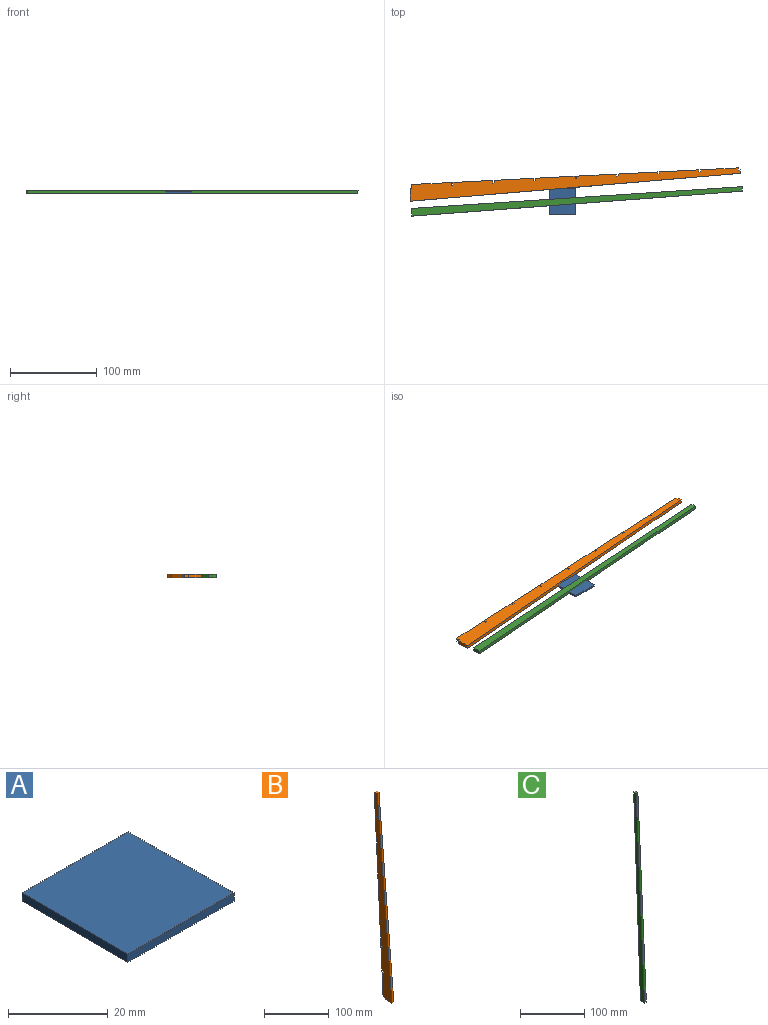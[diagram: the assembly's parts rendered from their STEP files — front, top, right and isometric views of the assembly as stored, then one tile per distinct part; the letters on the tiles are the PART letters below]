
ASSEMBLY  parts=3 mates=2
PART A: 6 faces, bbox 30x30x2 mm
  f0: plane 30x2mm, normal (-1,0,0), area 60mm2, adj f1,f3,f4,f5
  f1: plane 30x2mm, normal (0,-1,0), area 60mm2, adj f0,f2,f4,f5
  f2: plane 30x2mm, normal (1,0,0), area 60mm2, adj f1,f3,f4,f5
  f3: plane 30x2mm, normal (0,1,0), area 60mm2, adj f0,f2,f4,f5
  f4: plane 30x30mm, normal (0,0,1), area 900mm2, adj f0,f1,f2,f3
  f5: plane 30x30mm, normal (0,0,-1), area 900mm2, adj f0,f1,f2,f3
PART B: 38 faces, bbox 5.5x39.9x381.5 mm
  f0: plane 14.29x4mm, normal (0,0,-1), area 57.2mm2, adj f1,f5,f23,f37
  f1: plane 380.01x38.38mm, normal (1,0,0), area 4815.4mm2, adj f0,f2,f3,f4,f6,f7,f8,f9
  f2: plane 4x3.85mm, normal (0,0,1), area 15.4mm2, adj f1,f5,f22,f37
  f3: plane 4x2.7mm, normal (0,0,1), area 10.8mm2, adj f1,f5,f28,f29
  f4: plane 4x1.88mm, normal (0,0,1), area 7.5mm2, adj f1,f5,f34,f35
  f5: plane 381.51x39.88mm, normal (-1,0,0), area 4816mm2, adj f0,f2,f3,f4,f6,f7,f8,f9
  f6: plane 4x2.6mm, normal (0,0,1), area 10.4mm2, adj f1,f5,f21,f22
  f7: plane 4.76x4mm, normal (0,0,-1), area 19mm2, adj f1,f5,f23,f24
  f8: plane 4x3.43mm, normal (0,0,1), area 13.7mm2, adj f1,f5,f24,f25
  f9: plane 4x3.4mm, normal (0,0,-1), area 13.6mm2, adj f1,f5,f25,f26
  f10: plane 4x3.03mm, normal (0,0,-1), area 12.1mm2, adj f1,f5,f27,f28
  f11: plane 4x3.07mm, normal (0,0,1), area 12.3mm2, adj f1,f5,f26,f27
  f12: plane 4x2.66mm, normal (0,0,-1), area 10.7mm2, adj f1,f5,f29,f30
  f13: plane 4x2.62mm, normal (0,0,-1), area 10.5mm2, adj f1,f5,f31,f32
  f14: plane 4x2.66mm, normal (0,0,1), area 10.6mm2, adj f1,f5,f30,f31
  f15: plane 4x2.24mm, normal (0,0,-1), area 9mm2, adj f1,f5,f33,f34
  f16: plane 4x2.27mm, normal (0,0,1), area 9.1mm2, adj f1,f5,f32,f33
  f17: plane 4x1.85mm, normal (0,0,-1), area 7.4mm2, adj f1,f5,f35,f36
  f18: plane 4x2.12mm, normal (0,0,-1), area 8.5mm2, adj f1,f5,f20,f21
  f19: plane 4x2.15mm, normal (0,0,1), area 8.6mm2, adj f1,f5,f20,f36
  f20: plane 4x2mm, normal (0,1,-0.07), area 8mm2, adj f1,f5,f18,f19
  f21: extruded ~43.5x4mm, area 174.2mm2, adj f1,f5,f6,f18
  f22: plane 4x2mm, normal (0,1,-0.07), area 8mm2, adj f1,f2,f5,f6
  f23: plane 4x2mm, normal (0,1,-0.07), area 8mm2, adj f0,f1,f5,f7
  f24: extruded ~45.5x4mm, area 182.2mm2, adj f1,f5,f7,f8
  f25: plane 4x2mm, normal (0,1,-0.07), area 8mm2, adj f1,f5,f8,f9
  f26: extruded ~45.5x4mm, area 182.2mm2, adj f1,f5,f9,f11
  f27: plane 4x2mm, normal (0,1,-0.07), area 8mm2, adj f1,f5,f10,f11
  f28: extruded ~45.5x4mm, area 182.2mm2, adj f1,f3,f5,f10
  f29: plane 4x2mm, normal (0,1,-0.07), area 8mm2, adj f1,f3,f5,f12
  f30: extruded ~45.5x4mm, area 182.2mm2, adj f1,f5,f12,f14
  f31: plane 4x2mm, normal (0,1,-0.07), area 8mm2, adj f1,f5,f13,f14
  f32: extruded ~45.5x4mm, area 182.2mm2, adj f1,f5,f13,f16
  f33: plane 4x2mm, normal (0,1,-0.07), area 8mm2, adj f1,f5,f15,f16
  f34: extruded ~45.5x4mm, area 182.2mm2, adj f1,f4,f5,f15
  f35: plane 4x2mm, normal (0,1,-0.07), area 8mm2, adj f1,f4,f5,f17
  f36: extruded ~45.5x4mm, area 182.2mm2, adj f1,f5,f17,f19
  f37: extruded ~380x32.07mm, area 1525.4mm2, adj f0,f1,f2,f5
PART C: 6 faces, bbox 14x33.9x380.1 mm
  f0: extruded ~380.11x28.68mm, area 1524.8mm2, adj f1,f3,f4,f5
  f1: plane 8.9x4mm, normal (-0.03,0,-1), area 35.6mm2, adj f0,f2,f4,f5
  f2: extruded ~380.11x24.98mm, area 1523.8mm2, adj f1,f3,f4,f5
  f3: plane 5.21x4mm, normal (0.03,0,1), area 20.8mm2, adj f0,f2,f4,f5
  f4: plane 380x33.89mm, normal (-1,0,0.03), area 2727.1mm2, adj f0,f1,f2,f3
  f5: plane 380x33.89mm, normal (1,0,-0.03), area 2727.1mm2, adj f0,f1,f2,f3
PLACE A at identity fixed
PLACE B rot(axis=(0,1,0),90deg) t=(-175.97,4,57.2)mm
PLACE C rot(axis=(0,1,0),88.5deg) t=(-173.93,-12.81,4)mm
MATE planar C.f5 <-> A.f5  axis (0,0,-1) through (0,0,0)mm
MATE parallel A.f5 <-> B.f1  axis (0,0,-1) through (0,0,0)mm
